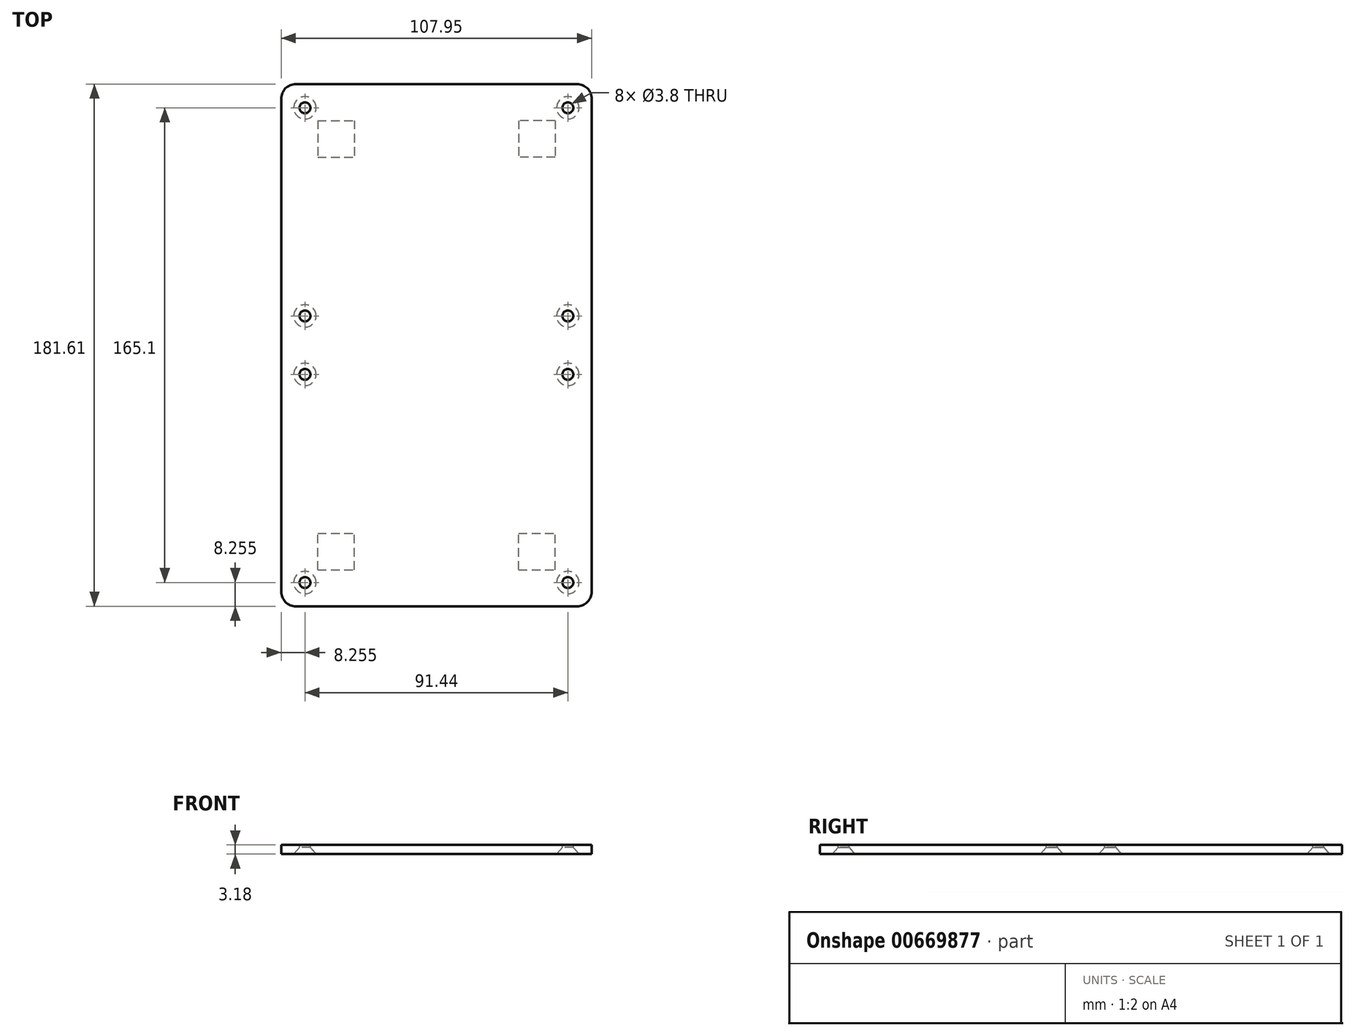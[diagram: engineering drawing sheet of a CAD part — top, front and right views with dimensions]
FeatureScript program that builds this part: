
annotation { "Feature Type Name" : "Feature", "Feature Type Description" : "" }
export const myFeature = defineFeature(function(context is Context, id is Id, definition is map)
    precondition{}
    {
        {
            var Q0;
            Q0=qCreatedBy(makeId("Top.planeOp"),FACE);
            var sketch = newSketch(context, id + "F0", { "sketchPlane" : qUnion([Q0])});
            skLineSegment(sketch, "E0.bottom", {"start": v(0, 0) * mm, "end": v(107.95, 0) * mm});
            skLineSegment(sketch, "E0.top", {"start": v(0, 181.61) * mm, "end": v(107.95, 181.61) * mm});
            skLineSegment(sketch, "E0.left", {"start": v(0, 0) * mm, "end": v(0, 181.61) * mm});
            skLineSegment(sketch, "E0.right", {"start": v(107.95, 0) * mm, "end": v(107.95, 181.61) * mm});
            skSolve(sketch);
        }
        {
            var Q0;
            Q0=qSketchRegion(id+"F0",true);
            extrude(context, id + "F1", {"entities" : qUnion([Q0]), "depth" : 3.17 * mm});
        }
        {
            var Q0;
            Q0=makeQuery(id+"F1.opExtrude","CAP_FACE",FACE,{"disambiguationData":[OSD([sQuery(id+"F0.wireOp",EDGE,"E0.bottom"),sQuery(id+"F0.wireOp",EDGE,"E0.top"),sQuery(id+"F0.wireOp",EDGE,"E0.left"),sQuery(id+"F0.wireOp",EDGE,"E0.right")])],"isStart":true});
            var sketch = newSketch(context, id + "F2", { "sketchPlane" : qUnion([Q0])});
            skPoint(sketch, "E1", {"position": v(8.26, -173.36) * mm});
            skPoint(sketch, "E2", {"position": v(8.26, -100.97) * mm});
            skPoint(sketch, "E3", {"position": v(8.26, -80.64) * mm});
            skPoint(sketch, "E4", {"position": v(8.26, -8.26) * mm});
            skPoint(sketch, "E5", {"position": v(99.7, -8.26) * mm});
            skPoint(sketch, "E6", {"position": v(99.7, -80.64) * mm});
            skPoint(sketch, "E7", {"position": v(99.7, -100.97) * mm});
            skPoint(sketch, "E8", {"position": v(99.7, -173.36) * mm});
            skSolve(sketch);
        }
        {
            var Q0;
            Q0=sQuery(id+"F2.wireOp",VERTEX,"E4");
            var Q1;
            Q1=sQuery(id+"F2.wireOp",VERTEX,"E5");
            var Q2;
            Q2=sQuery(id+"F2.wireOp",VERTEX,"E6");
            var Q3;
            Q3=sQuery(id+"F2.wireOp",VERTEX,"E3");
            var Q4;
            Q4=sQuery(id+"F2.wireOp",VERTEX,"E2");
            var Q5;
            Q5=sQuery(id+"F2.wireOp",VERTEX,"E1");
            var Q6;
            Q6=sQuery(id+"F2.wireOp",VERTEX,"E8");
            var Q7;
            Q7=sQuery(id+"F2.wireOp",VERTEX,"E7");
            var Q8;
            Q8=makeQuery(id+"F1.opExtrude","SWEPT_BODY",BODY,{"disambiguationData":[OSD([sQuery(id+"F0.wireOp",EDGE,"E0.bottom"),sQuery(id+"F0.wireOp",EDGE,"E0.top"),sQuery(id+"F0.wireOp",EDGE,"E0.left"),sQuery(id+"F0.wireOp",EDGE,"E0.right")])]});
            hole(context, id + "F3", {"style" : HoleStyle.C_SINK, "endStyle" : HoleEndStyle.THROUGH, "standardTappedOrClearance" : lookupTablePath({ "standard" : "ANSI", "fit" : "Normal (ASME)", "size" : "#6", "type" : "Clearance" }), "standardBlindInLast" : lookupTablePath({ "fit" : "Free", "standard" : "ANSI", "size" : "#6", "type" : "Clearance" }), "holeDiameter" : 3.8 * mm, "cSinkDiameter" : 7.8 * mm, "cSinkAngle" : 82 * degree, "tappedDepth" : 2.77 * mm, "tapClearance" : 3, "startFromSketch" : true, "locations" : qUnion([Q0, Q1, Q2, Q3, Q4, Q5, Q6, Q7]), "scope" : qUnion([Q8])});
        }
        {
            var Q0;
            Q0=makeQuery(id+"F1.opExtrude","SWEPT_EDGE",EDGE,{"disambiguationData":[OSD([sQuery(id+"F0.wireOp",EDGE,"E0.bottom"),sQuery(id+"F0.wireOp",EDGE,"E0.left")])]});
            var Q1;
            Q1=makeQuery(id+"F1.opExtrude","SWEPT_EDGE",EDGE,{"disambiguationData":[OSD([sQuery(id+"F0.wireOp",EDGE,"E0.bottom"),sQuery(id+"F0.wireOp",EDGE,"E0.right")])]});
            var Q2;
            Q2=makeQuery(id+"F1.opExtrude","SWEPT_EDGE",EDGE,{"disambiguationData":[OSD([sQuery(id+"F0.wireOp",EDGE,"E0.top"),sQuery(id+"F0.wireOp",EDGE,"E0.right")])]});
            var Q3;
            Q3=makeQuery(id+"F1.opExtrude","SWEPT_EDGE",EDGE,{"disambiguationData":[OSD([sQuery(id+"F0.wireOp",EDGE,"E0.top"),sQuery(id+"F0.wireOp",EDGE,"E0.left")])]});
            fillet(context, id + "F4", {"entities" : qUnion([Q0, Q1, Q2, Q3]), "radius" : 5.08 * mm, "tangentPropagation" : true, "allowEdgeOverflow" : false});
        }
        {
            var Q0;
            Q0=makeQuery(id+"F1.opExtrude","CAP_FACE",FACE,{"disambiguationData":[OSD([sQuery(id+"F0.wireOp",EDGE,"E0.bottom"),sQuery(id+"F0.wireOp",EDGE,"E0.top"),sQuery(id+"F0.wireOp",EDGE,"E0.left"),sQuery(id+"F0.wireOp",EDGE,"E0.right")])],"isStart":true});
            var sketch = newSketch(context, id + "F5", { "sketchPlane" : qUnion([Q0])});
            skLineSegment(sketch, "E9.bottom", {"start": v(12.7, -12.7) * mm, "end": v(25.4, -12.7) * mm});
            skLineSegment(sketch, "E9.top", {"start": v(12.7, -25.4) * mm, "end": v(25.4, -25.4) * mm});
            skLineSegment(sketch, "E9.left", {"start": v(12.7, -12.7) * mm, "end": v(12.7, -25.4) * mm});
            skLineSegment(sketch, "E9.right", {"start": v(25.4, -12.7) * mm, "end": v(25.4, -25.4) * mm});
            skPoint(sketch, "E10.oppositeSnap0", {"position": v(25.4, -19.05) * mm});
            skLineSegment(sketch, "E11.bottom", {"start": v(82.55, -12.7) * mm, "end": v(95.25, -12.7) * mm});
            skLineSegment(sketch, "E11.top", {"start": v(82.55, -25.4) * mm, "end": v(95.25, -25.4) * mm});
            skLineSegment(sketch, "E11.left", {"start": v(82.55, -12.7) * mm, "end": v(82.55, -25.4) * mm});
            skLineSegment(sketch, "E11.right", {"start": v(95.25, -12.7) * mm, "end": v(95.25, -25.4) * mm});
            skLineSegment(sketch, "E12.bottom", {"start": v(12.7, -168.91) * mm, "end": v(25.4, -168.91) * mm});
            skLineSegment(sketch, "E12.top", {"start": v(12.7, -156.21) * mm, "end": v(25.4, -156.21) * mm});
            skLineSegment(sketch, "E12.left", {"start": v(12.7, -168.91) * mm, "end": v(12.7, -156.21) * mm});
            skLineSegment(sketch, "E12.right", {"start": v(25.4, -168.91) * mm, "end": v(25.4, -156.21) * mm});
            skLineSegment(sketch, "E13.bottom", {"start": v(95.25, -168.91) * mm, "end": v(82.55, -168.91) * mm});
            skLineSegment(sketch, "E13.top", {"start": v(95.25, -156.21) * mm, "end": v(82.55, -156.21) * mm});
            skLineSegment(sketch, "E13.left", {"start": v(95.25, -168.91) * mm, "end": v(95.25, -156.21) * mm});
            skLineSegment(sketch, "E13.right", {"start": v(82.55, -168.91) * mm, "end": v(82.55, -156.21) * mm});
            skSolve(sketch);
        }
        {
            var Q0;
            Q0 = qSketchRegion(id + "F5", true);
            extrude(context, id + "F6", {"entities" : qUnion([Q0]), "operationType" : NewBodyOperationType.REMOVE, "oppositeDirection" : true, "depth" : 0.13 * mm, "offsetDistance" : 25.4 * mm});
        }
    });
